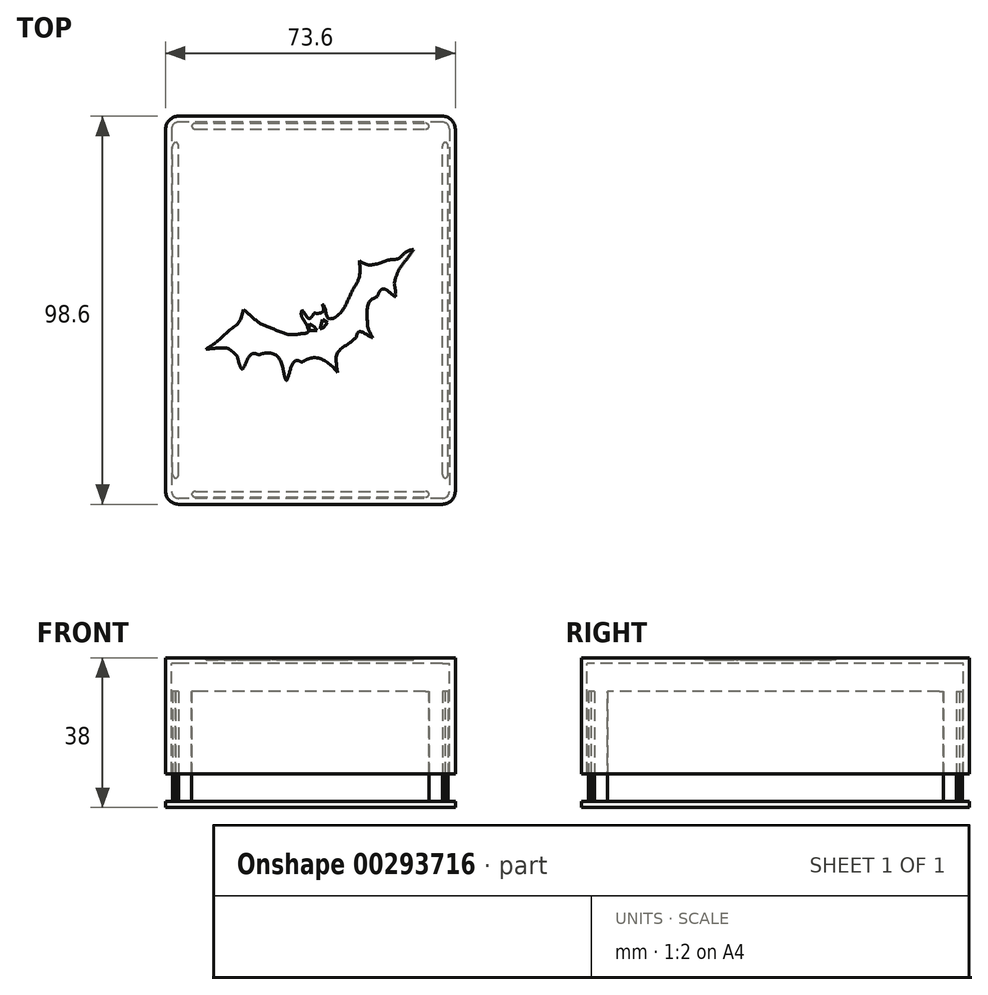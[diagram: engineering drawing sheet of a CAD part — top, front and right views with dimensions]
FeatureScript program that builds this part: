
annotation { "Feature Type Name" : "Feature", "Feature Type Description" : "" }
export const myFeature = defineFeature(function(context is Context, id is Id, definition is map)
    precondition{}
    {
        {
            assignVariable(context, id + "F0", {"name" : "DeckDepth", "anyValue" : 28});
        }
        {
            var Q0;
            Q0=qCreatedBy(makeId("Top.planeOp"),FACE);
            var sketch = newSketch(context, id + "F1", { "sketchPlane" : qUnion([Q0])});
            skLineSegment(sketch, "E0.bottom", {"start": v(33.5, 46) * mm, "end": v(-33.5, 46) * mm});
            skLineSegment(sketch, "E0.top", {"start": v(33.5, -46) * mm, "end": v(-33.5, -46) * mm});
            skLineSegment(sketch, "E0.left", {"start": v(33.5, 46) * mm, "end": v(33.5, -46) * mm});
            skLineSegment(sketch, "E0.right", {"start": v(-33.5, 46) * mm, "end": v(-33.5, -46) * mm});
            skPoint(sketch, "E0.middle", {"position": v(0, 0) * mm});
            skLineSegment(sketch, "E1.0", {"start": v(-35, 47.5) * mm, "end": v(-35, -47.5) * mm});
            skLineSegment(sketch, "E1.1", {"start": v(35, 47.5) * mm, "end": v(-35, 47.5) * mm});
            skLineSegment(sketch, "E1.2", {"start": v(35, 47.5) * mm, "end": v(35, -47.5) * mm});
            skLineSegment(sketch, "E1.3", {"start": v(35, -47.5) * mm, "end": v(-35, -47.5) * mm});
            skLineSegment(sketch, "E2.0", {"start": v(-36.8, 49.3) * mm, "end": v(-36.8, -49.3) * mm});
            skLineSegment(sketch, "E2.1", {"start": v(36.8, 49.3) * mm, "end": v(-36.8, 49.3) * mm});
            skLineSegment(sketch, "E2.2", {"start": v(36.8, 49.3) * mm, "end": v(36.8, -49.3) * mm});
            skLineSegment(sketch, "E2.3", {"start": v(36.8, -49.3) * mm, "end": v(-36.8, -49.3) * mm});
            skCircle(sketch, "E3", {"center": v(33.5, 46) * mm, "radius": 3.3 * mm});
            skCircle(sketch, "E4", {"center": v(33.5, 46) * mm, "radius": 1.5 * mm});
            skLineSegment(sketch, "E5", {"start": v(30.2, 46) * mm, "end": v(30.2, 47.5) * mm});
            skLineSegment(sketch, "E6", {"start": v(33.5, 42.7) * mm, "end": v(35, 42.7) * mm});
            skCircle(sketch, "E7", {"center": v(-33.5, 46) * mm, "radius": 3.3 * mm});
            skCircle(sketch, "E8", {"center": v(-33.5, 46) * mm, "radius": 1.5 * mm});
            skLineSegment(sketch, "E9", {"start": v(-30.2, 46) * mm, "end": v(-30.2, 47.5) * mm});
            skLineSegment(sketch, "E10", {"start": v(-33.5, 42.7) * mm, "end": v(-35, 42.7) * mm});
            skCircle(sketch, "E11", {"center": v(-33.5, -46) * mm, "radius": 3.3 * mm});
            skCircle(sketch, "E12", {"center": v(-33.5, -46) * mm, "radius": 1.5 * mm});
            skLineSegment(sketch, "E13", {"start": v(-33.5, -42.7) * mm, "end": v(-35, -42.7) * mm});
            skLineSegment(sketch, "E14", {"start": v(-30.2, -46) * mm, "end": v(-30.2, -47.5) * mm});
            skCircle(sketch, "E15", {"center": v(33.5, -46) * mm, "radius": 3.3 * mm});
            skCircle(sketch, "E16", {"center": v(33.5, -46) * mm, "radius": 1.5 * mm});
            skLineSegment(sketch, "E17", {"start": v(30.2, -46) * mm, "end": v(30.2, -47.5) * mm});
            skLineSegment(sketch, "E18", {"start": v(33.5, -42.7) * mm, "end": v(35, -42.7) * mm});
            skSolve(sketch);
        }
        {
            var Q0;
            {var subQ1=sQuery(id+"F1.wireOp",EDGE,"E1.0");var subQ5=sQuery(id+"F1.wireOp",EDGE,"E11");var subQ6=makeQuery(id+"F1.imprint","INTERSECT",VERTEX,{"derivedFrom":[subQ1,subQ5]});Q0=makeQuery(id+"F1.imprint","IMPRINT",FACE,{"disambiguationData":[TD([[makeQuery(id+"F1.imprint","IMPRINT",EDGE,{"disambiguationData":[TD([[subQ6,-1.0]])],"derivedFrom":subQ1}),-1.0]])]});}
            var Q1;
            {var subQ5=sQuery(id+"F1.wireOp",EDGE,"E3");var subQ13=sQuery(id+"F1.wireOp",EDGE,"E0.bottom");var subQ14=makeQuery(id+"F1.imprint","INTERSECT",VERTEX,{"derivedFrom":[subQ13,subQ5,sQuery(id+"F1.wireOp",EDGE,"E5")]});Q1=makeQuery(id+"F1.imprint","IMPRINT",FACE,{"disambiguationData":[TD([[makeQuery(id+"F1.imprint","IMPRINT",EDGE,{"disambiguationData":[TD([[subQ14,-1.0]])],"derivedFrom":subQ13}),1.0]])]});}
            var Q2;
            {var subQ0=sQuery(id+"F1.wireOp",EDGE,"E6");Q2=makeQuery(id+"F1.imprint","IMPRINT",FACE,{"disambiguationData":[TD([[makeQuery(id+"F1.imprint","IMPRINT",EDGE,{"derivedFrom":subQ0}),-1.0]])]});}
            var Q3;
            {var subQ0=sQuery(id+"F1.wireOp",EDGE,"E10");Q3=makeQuery(id+"F1.imprint","IMPRINT",FACE,{"disambiguationData":[TD([[makeQuery(id+"F1.imprint","IMPRINT",EDGE,{"derivedFrom":subQ0}),1.0]])]});}
            var Q4;
            {var subQ5=sQuery(id+"F1.wireOp",EDGE,"E1.2");var subQ8=makeQuery(id+"F1.imprint","INTERSECT",VERTEX,{"derivedFrom":[subQ5,sQuery(id+"F1.wireOp",EDGE,"E6")]});Q4=makeQuery(id+"F1.imprint","IMPRINT",FACE,{"disambiguationData":[TD([[makeQuery(id+"F1.imprint","IMPRINT",EDGE,{"disambiguationData":[TD([[subQ8,1.0]])],"derivedFrom":subQ5}),1.0]])]});}
            var Q5;
            {var subQ0=sQuery(id+"F1.wireOp",EDGE,"E1.3");var subQ8=makeQuery(id+"F1.imprint","INTERSECT",VERTEX,{"derivedFrom":[subQ0,sQuery(id+"F1.wireOp",EDGE,"E17")]});Q5=makeQuery(id+"F1.imprint","IMPRINT",FACE,{"disambiguationData":[TD([[makeQuery(id+"F1.imprint","IMPRINT",EDGE,{"disambiguationData":[TD([[subQ8,1.0]])],"derivedFrom":subQ0}),1.0]])]});}
            var Q6;
            {var subQ0=sQuery(id+"F1.wireOp",EDGE,"E5");Q6=makeQuery(id+"F1.imprint","IMPRINT",FACE,{"disambiguationData":[TD([[makeQuery(id+"F1.imprint","IMPRINT",EDGE,{"derivedFrom":subQ0}),1.0]])]});}
            var Q7;
            {var subQ1=sQuery(id+"F1.wireOp",EDGE,"E0.bottom");var subQ3=sQuery(id+"F1.wireOp",EDGE,"E4");var subQ4=makeQuery(id+"F1.imprint","INTERSECT",VERTEX,{"derivedFrom":[subQ1,subQ3]});Q7=makeQuery(id+"F1.imprint","IMPRINT",FACE,{"disambiguationData":[TD([[makeQuery(id+"F1.imprint","IMPRINT",EDGE,{"disambiguationData":[TD([[subQ4,-1.0]])],"derivedFrom":subQ3}),-1.0]])]});}
            var Q8;
            {var subQ1=sQuery(id+"F1.wireOp",EDGE,"E1.2");var subQ5=sQuery(id+"F1.wireOp",EDGE,"E1.1");var subQ6=makeQuery(id+"F1.imprint","INTERSECT",VERTEX,{"derivedFrom":[subQ5,subQ1]});Q8=makeQuery(id+"F1.imprint","IMPRINT",FACE,{"disambiguationData":[TD([[makeQuery(id+"F1.imprint","IMPRINT",EDGE,{"disambiguationData":[TD([[subQ6,-1.0]])],"derivedFrom":subQ5}),-1.0]])]});}
            var Q9;
            {var subQ0=sQuery(id+"F1.wireOp",EDGE,"E14");Q9=makeQuery(id+"F1.imprint","IMPRINT",FACE,{"disambiguationData":[TD([[makeQuery(id+"F1.imprint","IMPRINT",EDGE,{"derivedFrom":subQ0}),1.0]])]});}
            var Q10;
            {var subQ0=sQuery(id+"F1.wireOp",EDGE,"E1.1");var subQ1=sQuery(id+"F1.wireOp",EDGE,"E1.0");var subQ2=makeQuery(id+"F1.imprint","INTERSECT",VERTEX,{"derivedFrom":[subQ1,subQ0]});Q10=makeQuery(id+"F1.imprint","IMPRINT",FACE,{"disambiguationData":[TD([[makeQuery(id+"F1.imprint","IMPRINT",EDGE,{"disambiguationData":[TD([[subQ2,-1.0]])],"derivedFrom":subQ1}),-1.0]])]});}
            var Q11;
            {var subQ1=sQuery(id+"F1.wireOp",EDGE,"E0.top");var subQ3=sQuery(id+"F1.wireOp",EDGE,"E16");var subQ4=makeQuery(id+"F1.imprint","INTERSECT",VERTEX,{"derivedFrom":[subQ1,subQ3]});Q11=makeQuery(id+"F1.imprint","IMPRINT",FACE,{"disambiguationData":[TD([[makeQuery(id+"F1.imprint","IMPRINT",EDGE,{"disambiguationData":[TD([[subQ4,1.0]])],"derivedFrom":subQ3}),-1.0]])]});}
            var Q12;
            {var subQ5=sQuery(id+"F1.wireOp",EDGE,"E1.0");var subQ8=makeQuery(id+"F1.imprint","INTERSECT",VERTEX,{"derivedFrom":[subQ5,sQuery(id+"F1.wireOp",EDGE,"E10")]});Q12=makeQuery(id+"F1.imprint","IMPRINT",FACE,{"disambiguationData":[TD([[makeQuery(id+"F1.imprint","IMPRINT",EDGE,{"disambiguationData":[TD([[subQ8,1.0]])],"derivedFrom":subQ5}),-1.0]])]});}
            var Q13;
            {var subQ1=sQuery(id+"F1.wireOp",EDGE,"E0.bottom");var subQ3=sQuery(id+"F1.wireOp",EDGE,"E8");var subQ4=makeQuery(id+"F1.imprint","INTERSECT",VERTEX,{"derivedFrom":[subQ1,subQ3]});Q13=makeQuery(id+"F1.imprint","IMPRINT",FACE,{"disambiguationData":[TD([[makeQuery(id+"F1.imprint","IMPRINT",EDGE,{"disambiguationData":[TD([[subQ4,1.0]])],"derivedFrom":subQ3}),-1.0]])]});}
            var Q14;
            {var subQ1=sQuery(id+"F1.wireOp",EDGE,"E0.top");var subQ3=sQuery(id+"F1.wireOp",EDGE,"E12");var subQ4=makeQuery(id+"F1.imprint","INTERSECT",VERTEX,{"derivedFrom":[subQ1,subQ3]});Q14=makeQuery(id+"F1.imprint","IMPRINT",FACE,{"disambiguationData":[TD([[makeQuery(id+"F1.imprint","IMPRINT",EDGE,{"disambiguationData":[TD([[subQ4,-1.0]])],"derivedFrom":subQ3}),-1.0]])]});}
            var Q15;
            {var subQ5=sQuery(id+"F1.wireOp",EDGE,"E1.1");var subQ6=makeQuery(id+"F1.imprint","INTERSECT",VERTEX,{"derivedFrom":[subQ5,sQuery(id+"F1.wireOp",EDGE,"E5")]});Q15=makeQuery(id+"F1.imprint","IMPRINT",FACE,{"disambiguationData":[TD([[makeQuery(id+"F1.imprint","IMPRINT",EDGE,{"disambiguationData":[TD([[subQ6,1.0]])],"derivedFrom":subQ5}),-1.0]])]});}
            var Q16;
            {var subQ0=sQuery(id+"F1.wireOp",EDGE,"E7");var subQ5=sQuery(id+"F1.wireOp",EDGE,"E1.1");var subQ7=makeQuery(id+"F1.imprint","INTERSECT",VERTEX,{"derivedFrom":[subQ5,subQ0]});Q16=makeQuery(id+"F1.imprint","IMPRINT",FACE,{"disambiguationData":[TD([[makeQuery(id+"F1.imprint","IMPRINT",EDGE,{"disambiguationData":[TD([[subQ7,-1.0]])],"derivedFrom":subQ5}),1.0]])]});}
            var Q17;
            {var subQ3=sQuery(id+"F1.wireOp",EDGE,"E15");var subQ5=sQuery(id+"F1.wireOp",EDGE,"E1.2");var subQ8=makeQuery(id+"F1.imprint","INTERSECT",VERTEX,{"derivedFrom":[subQ5,subQ3]});Q17=makeQuery(id+"F1.imprint","IMPRINT",FACE,{"disambiguationData":[TD([[makeQuery(id+"F1.imprint","IMPRINT",EDGE,{"disambiguationData":[TD([[subQ8,-1.0]])],"derivedFrom":subQ5}),1.0]])]});}
            var Q18;
            {var subQ1=sQuery(id+"F1.wireOp",EDGE,"E0.bottom");var subQ5=sQuery(id+"F1.wireOp",EDGE,"E0.left");var subQ6=makeQuery(id+"F1.imprint","INTERSECT",VERTEX,{"derivedFrom":[subQ1,subQ5]});Q18=makeQuery(id+"F1.imprint","IMPRINT",FACE,{"disambiguationData":[TD([[makeQuery(id+"F1.imprint","IMPRINT",EDGE,{"disambiguationData":[TD([[subQ6,-1.0]])],"derivedFrom":subQ1}),-1.0]])]});}
            var Q19;
            {var subQ0=sQuery(id+"F1.wireOp",EDGE,"E11");var subQ5=sQuery(id+"F1.wireOp",EDGE,"E1.3");var subQ7=makeQuery(id+"F1.imprint","INTERSECT",VERTEX,{"derivedFrom":[subQ5,subQ0]});Q19=makeQuery(id+"F1.imprint","IMPRINT",FACE,{"disambiguationData":[TD([[makeQuery(id+"F1.imprint","IMPRINT",EDGE,{"disambiguationData":[TD([[subQ7,-1.0]])],"derivedFrom":subQ5}),-1.0]])]});}
            var Q20;
            {var subQ0=sQuery(id+"F1.wireOp",EDGE,"E15");var subQ5=sQuery(id+"F1.wireOp",EDGE,"E1.2");var subQ6=makeQuery(id+"F1.imprint","INTERSECT",VERTEX,{"derivedFrom":[subQ5,subQ0]});Q20=makeQuery(id+"F1.imprint","IMPRINT",FACE,{"disambiguationData":[TD([[makeQuery(id+"F1.imprint","IMPRINT",EDGE,{"disambiguationData":[TD([[subQ6,-1.0]])],"derivedFrom":subQ5}),-1.0]])]});}
            var Q21;
            {var subQ3=sQuery(id+"F1.wireOp",EDGE,"E4");var subQ5=sQuery(id+"F1.wireOp",EDGE,"E1.1");var subQ6=makeQuery(id+"F1.imprint","INTERSECT",VERTEX,{"derivedFrom":[subQ5,subQ3]});Q21=makeQuery(id+"F1.imprint","IMPRINT",FACE,{"disambiguationData":[TD([[makeQuery(id+"F1.imprint","IMPRINT",EDGE,{"disambiguationData":[TD([[subQ6,-1.0]])],"derivedFrom":subQ5}),1.0]])]});}
            var Q22;
            {var subQ1=sQuery(id+"F1.wireOp",EDGE,"E0.bottom");var subQ4=sQuery(id+"F1.wireOp",EDGE,"E0.right");var subQ5=makeQuery(id+"F1.imprint","INTERSECT",VERTEX,{"derivedFrom":[subQ1,subQ4]});Q22=makeQuery(id+"F1.imprint","IMPRINT",FACE,{"disambiguationData":[TD([[makeQuery(id+"F1.imprint","IMPRINT",EDGE,{"disambiguationData":[TD([[subQ5,1.0]])],"derivedFrom":subQ1}),-1.0]])]});}
            var Q23;
            {var subQ3=sQuery(id+"F1.wireOp",EDGE,"E16");var subQ5=sQuery(id+"F1.wireOp",EDGE,"E1.3");var subQ6=makeQuery(id+"F1.imprint","INTERSECT",VERTEX,{"derivedFrom":[subQ5,subQ3]});Q23=makeQuery(id+"F1.imprint","IMPRINT",FACE,{"disambiguationData":[TD([[makeQuery(id+"F1.imprint","IMPRINT",EDGE,{"disambiguationData":[TD([[subQ6,-1.0]])],"derivedFrom":subQ5}),-1.0]])]});}
            var Q24;
            {var subQ0=sQuery(id+"F1.wireOp",EDGE,"E6");Q24=makeQuery(id+"F1.imprint","IMPRINT",FACE,{"disambiguationData":[TD([[makeQuery(id+"F1.imprint","IMPRINT",EDGE,{"derivedFrom":subQ0}),1.0]])]});}
            var Q25;
            {var subQ0=sQuery(id+"F1.wireOp",EDGE,"E0.right");var subQ1=sQuery(id+"F1.wireOp",EDGE,"E0.top");var subQ2=makeQuery(id+"F1.imprint","INTERSECT",VERTEX,{"derivedFrom":[subQ1,subQ0]});Q25=makeQuery(id+"F1.imprint","IMPRINT",FACE,{"disambiguationData":[TD([[makeQuery(id+"F1.imprint","IMPRINT",EDGE,{"disambiguationData":[TD([[subQ2,1.0]])],"derivedFrom":subQ1}),-1.0]])]});}
            var Q26;
            {var subQ0=sQuery(id+"F1.wireOp",EDGE,"E0.left");var subQ1=sQuery(id+"F1.wireOp",EDGE,"E0.top");var subQ2=makeQuery(id+"F1.imprint","INTERSECT",VERTEX,{"derivedFrom":[subQ1,subQ0]});Q26=makeQuery(id+"F1.imprint","IMPRINT",FACE,{"disambiguationData":[TD([[makeQuery(id+"F1.imprint","IMPRINT",EDGE,{"disambiguationData":[TD([[subQ2,-1.0]])],"derivedFrom":subQ1}),-1.0]])]});}
            var Q27;
            {var subQ0=sQuery(id+"F1.wireOp",EDGE,"E11");var subQ5=sQuery(id+"F1.wireOp",EDGE,"E1.0");var subQ6=makeQuery(id+"F1.imprint","INTERSECT",VERTEX,{"derivedFrom":[subQ5,subQ0]});Q27=makeQuery(id+"F1.imprint","IMPRINT",FACE,{"disambiguationData":[TD([[makeQuery(id+"F1.imprint","IMPRINT",EDGE,{"disambiguationData":[TD([[subQ6,-1.0]])],"derivedFrom":subQ5}),1.0]])]});}
            var Q28;
            {var subQ3=sQuery(id+"F1.wireOp",EDGE,"E8");var subQ5=sQuery(id+"F1.wireOp",EDGE,"E1.0");var subQ6=makeQuery(id+"F1.imprint","INTERSECT",VERTEX,{"derivedFrom":[subQ5,subQ3]});Q28=makeQuery(id+"F1.imprint","IMPRINT",FACE,{"disambiguationData":[TD([[makeQuery(id+"F1.imprint","IMPRINT",EDGE,{"disambiguationData":[TD([[subQ6,-1.0]])],"derivedFrom":subQ5}),1.0]])]});}
            var Q29;
            {var subQ3=sQuery(id+"F1.wireOp",EDGE,"E0.right");var subQ5=sQuery(id+"F1.wireOp",EDGE,"E0.top");var subQ6=makeQuery(id+"F1.imprint","INTERSECT",VERTEX,{"derivedFrom":[subQ5,subQ3]});Q29=makeQuery(id+"F1.imprint","IMPRINT",FACE,{"disambiguationData":[TD([[makeQuery(id+"F1.imprint","IMPRINT",EDGE,{"disambiguationData":[TD([[subQ6,1.0]])],"derivedFrom":subQ5}),1.0]])]});}
            var Q30;
            {var subQ3=sQuery(id+"F1.wireOp",EDGE,"E4");var subQ5=sQuery(id+"F1.wireOp",EDGE,"E1.2");var subQ6=makeQuery(id+"F1.imprint","INTERSECT",VERTEX,{"derivedFrom":[subQ5,subQ3]});Q30=makeQuery(id+"F1.imprint","IMPRINT",FACE,{"disambiguationData":[TD([[makeQuery(id+"F1.imprint","IMPRINT",EDGE,{"disambiguationData":[TD([[subQ6,-1.0]])],"derivedFrom":subQ5}),-1.0]])]});}
            var Q31;
            {var subQ0=sQuery(id+"F1.wireOp",EDGE,"E14");Q31=makeQuery(id+"F1.imprint","IMPRINT",FACE,{"disambiguationData":[TD([[makeQuery(id+"F1.imprint","IMPRINT",EDGE,{"derivedFrom":subQ0}),-1.0]])]});}
            var Q32;
            {var subQ0=sQuery(id+"F1.wireOp",EDGE,"E9");Q32=makeQuery(id+"F1.imprint","IMPRINT",FACE,{"disambiguationData":[TD([[makeQuery(id+"F1.imprint","IMPRINT",EDGE,{"derivedFrom":subQ0}),1.0]])]});}
            var Q33;
            {var subQ0=sQuery(id+"F1.wireOp",EDGE,"E5");Q33=makeQuery(id+"F1.imprint","IMPRINT",FACE,{"disambiguationData":[TD([[makeQuery(id+"F1.imprint","IMPRINT",EDGE,{"derivedFrom":subQ0}),-1.0]])]});}
            var Q34;
            {var subQ0=sQuery(id+"F1.wireOp",EDGE,"E13");Q34=makeQuery(id+"F1.imprint","IMPRINT",FACE,{"disambiguationData":[TD([[makeQuery(id+"F1.imprint","IMPRINT",EDGE,{"derivedFrom":subQ0}),1.0]])]});}
            var Q35;
            {var subQ0=sQuery(id+"F1.wireOp",EDGE,"E0.left");var subQ1=sQuery(id+"F1.wireOp",EDGE,"E0.bottom");var subQ2=makeQuery(id+"F1.imprint","INTERSECT",VERTEX,{"derivedFrom":[subQ1,subQ0]});Q35=makeQuery(id+"F1.imprint","IMPRINT",FACE,{"disambiguationData":[TD([[makeQuery(id+"F1.imprint","IMPRINT",EDGE,{"disambiguationData":[TD([[subQ2,-1.0]])],"derivedFrom":subQ1}),1.0]])]});}
            var Q36;
            {var subQ0=sQuery(id+"F1.wireOp",EDGE,"E1.1");var subQ1=sQuery(id+"F1.wireOp",EDGE,"E1.0");var subQ2=makeQuery(id+"F1.imprint","INTERSECT",VERTEX,{"derivedFrom":[subQ1,subQ0]});Q36=makeQuery(id+"F1.imprint","IMPRINT",FACE,{"disambiguationData":[TD([[makeQuery(id+"F1.imprint","IMPRINT",EDGE,{"disambiguationData":[TD([[subQ2,-1.0]])],"derivedFrom":subQ1}),1.0]])]});}
            var Q37;
            {var subQ0=sQuery(id+"F1.wireOp",EDGE,"E1.3");var subQ1=sQuery(id+"F1.wireOp",EDGE,"E1.0");var subQ2=makeQuery(id+"F1.imprint","INTERSECT",VERTEX,{"derivedFrom":[subQ1,subQ0]});Q37=makeQuery(id+"F1.imprint","IMPRINT",FACE,{"disambiguationData":[TD([[makeQuery(id+"F1.imprint","IMPRINT",EDGE,{"disambiguationData":[TD([[subQ2,1.0]])],"derivedFrom":subQ1}),1.0]])]});}
            var Q38;
            {var subQ0=sQuery(id+"F1.wireOp",EDGE,"E1.2");var subQ1=sQuery(id+"F1.wireOp",EDGE,"E1.1");var subQ2=makeQuery(id+"F1.imprint","INTERSECT",VERTEX,{"derivedFrom":[subQ1,subQ0]});Q38=makeQuery(id+"F1.imprint","IMPRINT",FACE,{"disambiguationData":[TD([[makeQuery(id+"F1.imprint","IMPRINT",EDGE,{"disambiguationData":[TD([[subQ2,-1.0]])],"derivedFrom":subQ1}),1.0]])]});}
            var Q39;
            {var subQ0=sQuery(id+"F1.wireOp",EDGE,"E1.3");var subQ1=sQuery(id+"F1.wireOp",EDGE,"E1.2");var subQ2=makeQuery(id+"F1.imprint","INTERSECT",VERTEX,{"derivedFrom":[subQ1,subQ0]});Q39=makeQuery(id+"F1.imprint","IMPRINT",FACE,{"disambiguationData":[TD([[makeQuery(id+"F1.imprint","IMPRINT",EDGE,{"disambiguationData":[TD([[subQ2,1.0]])],"derivedFrom":subQ1}),-1.0]])]});}
            var Q40;
            {var subQ0=sQuery(id+"F1.wireOp",EDGE,"E10");Q40=makeQuery(id+"F1.imprint","IMPRINT",FACE,{"disambiguationData":[TD([[makeQuery(id+"F1.imprint","IMPRINT",EDGE,{"derivedFrom":subQ0}),-1.0]])]});}
            var Q41;
            {var subQ1=sQuery(id+"F1.wireOp",EDGE,"E0.left");var subQ4=sQuery(id+"F1.wireOp",EDGE,"E0.top");var subQ5=makeQuery(id+"F1.imprint","INTERSECT",VERTEX,{"derivedFrom":[subQ4,subQ1]});Q41=makeQuery(id+"F1.imprint","IMPRINT",FACE,{"disambiguationData":[TD([[makeQuery(id+"F1.imprint","IMPRINT",EDGE,{"disambiguationData":[TD([[subQ5,-1.0]])],"derivedFrom":subQ4}),1.0]])]});}
            var Q42;
            {var subQ0=sQuery(id+"F1.wireOp",EDGE,"E18");Q42=makeQuery(id+"F1.imprint","IMPRINT",FACE,{"disambiguationData":[TD([[makeQuery(id+"F1.imprint","IMPRINT",EDGE,{"derivedFrom":subQ0}),-1.0]])]});}
            var Q43;
            {var subQ0=sQuery(id+"F1.wireOp",EDGE,"E17");Q43=makeQuery(id+"F1.imprint","IMPRINT",FACE,{"disambiguationData":[TD([[makeQuery(id+"F1.imprint","IMPRINT",EDGE,{"derivedFrom":subQ0}),1.0]])]});}
            var Q44;
            {var subQ0=sQuery(id+"F1.wireOp",EDGE,"E0.right");var subQ1=sQuery(id+"F1.wireOp",EDGE,"E0.bottom");var subQ2=makeQuery(id+"F1.imprint","INTERSECT",VERTEX,{"derivedFrom":[subQ1,subQ0]});Q44=makeQuery(id+"F1.imprint","IMPRINT",FACE,{"disambiguationData":[TD([[makeQuery(id+"F1.imprint","IMPRINT",EDGE,{"disambiguationData":[TD([[subQ2,1.0]])],"derivedFrom":subQ1}),1.0]])]});}
            extrude(context, id + "F2", {"entities" : qUnion([Q0, Q1, Q2, Q3, Q4, Q5, Q6, Q7, Q8, Q9, Q10, Q11, Q12, Q13, Q14, Q15, Q16, Q17, Q18, Q19, Q20, Q21, Q22, Q23, Q24, Q25, Q26, Q27, Q28, Q29, Q30, Q31, Q32, Q33, Q34, Q35, Q36, Q37, Q38, Q39, Q40, Q41, Q42, Q43, Q44]), "depth" : 1.5 * mm});
        }
        {
            var Q0;
            {var subQ0=sQuery(id+"F1.wireOp",EDGE,"E10");Q0=makeQuery(id+"F1.imprint","IMPRINT",FACE,{"disambiguationData":[TD([[makeQuery(id+"F1.imprint","IMPRINT",EDGE,{"derivedFrom":subQ0}),1.0]])]});}
            var Q1;
            {var subQ0=sQuery(id+"F1.wireOp",EDGE,"E5");Q1=makeQuery(id+"F1.imprint","IMPRINT",FACE,{"disambiguationData":[TD([[makeQuery(id+"F1.imprint","IMPRINT",EDGE,{"derivedFrom":subQ0}),1.0]])]});}
            var Q2;
            {var subQ0=sQuery(id+"F1.wireOp",EDGE,"E6");Q2=makeQuery(id+"F1.imprint","IMPRINT",FACE,{"disambiguationData":[TD([[makeQuery(id+"F1.imprint","IMPRINT",EDGE,{"derivedFrom":subQ0}),-1.0]])]});}
            var Q3;
            {var subQ0=sQuery(id+"F1.wireOp",EDGE,"E14");Q3=makeQuery(id+"F1.imprint","IMPRINT",FACE,{"disambiguationData":[TD([[makeQuery(id+"F1.imprint","IMPRINT",EDGE,{"derivedFrom":subQ0}),1.0]])]});}
            extrude(context, id + "F3", {"entities" : qUnion([Q0, Q1, Q2, Q3]), "operationType" : NewBodyOperationType.ADD, "depth" : (1.5 + getVariable(context, 'DeckDepth')) * mm});
        }
        {
            var Q0;
            Q0=makeQuery(id+"F3.opExtrude","SWEPT_EDGE",EDGE,{"disambiguationData":[OSD([sQuery(id+"F1.wireOp",EDGE,"E0.left"),sQuery(id+"F1.wireOp",EDGE,"E15"),sQuery(id+"F1.wireOp",EDGE,"E18")])]});
            var Q1;
            Q1=makeQuery(id+"F3.opExtrude","SWEPT_EDGE",EDGE,{"disambiguationData":[OSD([sQuery(id+"F1.wireOp",EDGE,"E1.2"),sQuery(id+"F1.wireOp",EDGE,"E18")])]});
            var Q2;
            Q2=makeQuery(id+"F3.opExtrude","SWEPT_EDGE",EDGE,{"disambiguationData":[OSD([sQuery(id+"F1.wireOp",EDGE,"E0.top"),sQuery(id+"F1.wireOp",EDGE,"E15"),sQuery(id+"F1.wireOp",EDGE,"E17")])]});
            var Q3;
            Q3=makeQuery(id+"F3.opExtrude","SWEPT_EDGE",EDGE,{"disambiguationData":[OSD([sQuery(id+"F1.wireOp",EDGE,"E1.3"),sQuery(id+"F1.wireOp",EDGE,"E17")])]});
            var Q4;
            Q4=makeQuery(id+"F3.opExtrude","SWEPT_EDGE",EDGE,{"disambiguationData":[OSD([sQuery(id+"F1.wireOp",EDGE,"E1.3"),sQuery(id+"F1.wireOp",EDGE,"E14")])]});
            var Q5;
            Q5=makeQuery(id+"F3.opExtrude","SWEPT_EDGE",EDGE,{"disambiguationData":[OSD([sQuery(id+"F1.wireOp",EDGE,"E0.top"),sQuery(id+"F1.wireOp",EDGE,"E11"),sQuery(id+"F1.wireOp",EDGE,"E14")])]});
            var Q6;
            Q6=makeQuery(id+"F3.opExtrude","SWEPT_EDGE",EDGE,{"disambiguationData":[OSD([sQuery(id+"F1.wireOp",EDGE,"E1.0"),sQuery(id+"F1.wireOp",EDGE,"E13")])]});
            var Q7;
            Q7=makeQuery(id+"F3.opExtrude","SWEPT_EDGE",EDGE,{"disambiguationData":[OSD([sQuery(id+"F1.wireOp",EDGE,"E0.right"),sQuery(id+"F1.wireOp",EDGE,"E11"),sQuery(id+"F1.wireOp",EDGE,"E13")])]});
            var Q8;
            Q8=makeQuery(id+"F3.opExtrude","SWEPT_EDGE",EDGE,{"disambiguationData":[OSD([sQuery(id+"F1.wireOp",EDGE,"E1.0"),sQuery(id+"F1.wireOp",EDGE,"E10")])]});
            var Q9;
            Q9=makeQuery(id+"F3.opExtrude","SWEPT_EDGE",EDGE,{"disambiguationData":[OSD([sQuery(id+"F1.wireOp",EDGE,"E0.right"),sQuery(id+"F1.wireOp",EDGE,"E7"),sQuery(id+"F1.wireOp",EDGE,"E10")])]});
            var Q10;
            Q10=makeQuery(id+"F3.opExtrude","SWEPT_EDGE",EDGE,{"disambiguationData":[OSD([sQuery(id+"F1.wireOp",EDGE,"E0.bottom"),sQuery(id+"F1.wireOp",EDGE,"E7"),sQuery(id+"F1.wireOp",EDGE,"E9")])]});
            var Q11;
            Q11=makeQuery(id+"F3.opExtrude","SWEPT_EDGE",EDGE,{"disambiguationData":[OSD([sQuery(id+"F1.wireOp",EDGE,"E1.1"),sQuery(id+"F1.wireOp",EDGE,"E9")])]});
            var Q12;
            Q12=makeQuery(id+"F3.opExtrude","SWEPT_EDGE",EDGE,{"disambiguationData":[OSD([sQuery(id+"F1.wireOp",EDGE,"E1.1"),sQuery(id+"F1.wireOp",EDGE,"E5")])]});
            var Q13;
            Q13=makeQuery(id+"F3.opExtrude","SWEPT_EDGE",EDGE,{"disambiguationData":[OSD([sQuery(id+"F1.wireOp",EDGE,"E0.bottom"),sQuery(id+"F1.wireOp",EDGE,"E3"),sQuery(id+"F1.wireOp",EDGE,"E5")])]});
            var Q14;
            Q14=makeQuery(id+"F3.opExtrude","SWEPT_EDGE",EDGE,{"disambiguationData":[OSD([sQuery(id+"F1.wireOp",EDGE,"E0.left"),sQuery(id+"F1.wireOp",EDGE,"E3"),sQuery(id+"F1.wireOp",EDGE,"E6")])]});
            var Q15;
            Q15=makeQuery(id+"F3.opExtrude","SWEPT_EDGE",EDGE,{"disambiguationData":[OSD([sQuery(id+"F1.wireOp",EDGE,"E1.2"),sQuery(id+"F1.wireOp",EDGE,"E6")])]});
            fillet(context, id + "F4", {"entities" : qUnion([Q0, Q1, Q2, Q3, Q4, Q5, Q6, Q7, Q8, Q9, Q10, Q11, Q12, Q13, Q14, Q15]), "radius" : 1 * mm, "tangentPropagation" : true, "allowEdgeOverflow" : false});
        }
        {
            var Q0;
            {var subQ5=sQuery(id+"F1.wireOp",EDGE,"E3");var subQ13=sQuery(id+"F1.wireOp",EDGE,"E0.bottom");var subQ14=makeQuery(id+"F1.imprint","INTERSECT",VERTEX,{"derivedFrom":[subQ13,subQ5,sQuery(id+"F1.wireOp",EDGE,"E5")]});Q0=makeQuery(id+"F1.imprint","IMPRINT",FACE,{"disambiguationData":[TD([[makeQuery(id+"F1.imprint","IMPRINT",EDGE,{"disambiguationData":[TD([[subQ14,-1.0]])],"derivedFrom":subQ13}),1.0]])]});}
            var Q1;
            {var subQ0=sQuery(id+"F1.wireOp",EDGE,"E1.1");var subQ1=sQuery(id+"F1.wireOp",EDGE,"E1.0");var subQ2=makeQuery(id+"F1.imprint","INTERSECT",VERTEX,{"derivedFrom":[subQ1,subQ0]});Q1=makeQuery(id+"F1.imprint","IMPRINT",FACE,{"disambiguationData":[TD([[makeQuery(id+"F1.imprint","IMPRINT",EDGE,{"disambiguationData":[TD([[subQ2,-1.0]])],"derivedFrom":subQ1}),-1.0]])]});}
            var Q2;
            {var subQ0=sQuery(id+"F1.wireOp",EDGE,"E1.3");var subQ8=makeQuery(id+"F1.imprint","INTERSECT",VERTEX,{"derivedFrom":[subQ0,sQuery(id+"F1.wireOp",EDGE,"E17")]});Q2=makeQuery(id+"F1.imprint","IMPRINT",FACE,{"disambiguationData":[TD([[makeQuery(id+"F1.imprint","IMPRINT",EDGE,{"disambiguationData":[TD([[subQ8,1.0]])],"derivedFrom":subQ0}),1.0]])]});}
            var Q3;
            {var subQ1=sQuery(id+"F1.wireOp",EDGE,"E0.bottom");var subQ3=sQuery(id+"F1.wireOp",EDGE,"E4");var subQ4=makeQuery(id+"F1.imprint","INTERSECT",VERTEX,{"derivedFrom":[subQ1,subQ3]});Q3=makeQuery(id+"F1.imprint","IMPRINT",FACE,{"disambiguationData":[TD([[makeQuery(id+"F1.imprint","IMPRINT",EDGE,{"disambiguationData":[TD([[subQ4,-1.0]])],"derivedFrom":subQ3}),-1.0]])]});}
            var Q4;
            {var subQ0=sQuery(id+"F1.wireOp",EDGE,"E5");Q4=makeQuery(id+"F1.imprint","IMPRINT",FACE,{"disambiguationData":[TD([[makeQuery(id+"F1.imprint","IMPRINT",EDGE,{"derivedFrom":subQ0}),1.0]])]});}
            var Q5;
            {var subQ1=sQuery(id+"F1.wireOp",EDGE,"E1.0");var subQ5=sQuery(id+"F1.wireOp",EDGE,"E11");var subQ6=makeQuery(id+"F1.imprint","INTERSECT",VERTEX,{"derivedFrom":[subQ1,subQ5]});Q5=makeQuery(id+"F1.imprint","IMPRINT",FACE,{"disambiguationData":[TD([[makeQuery(id+"F1.imprint","IMPRINT",EDGE,{"disambiguationData":[TD([[subQ6,-1.0]])],"derivedFrom":subQ1}),-1.0]])]});}
            var Q6;
            {var subQ0=sQuery(id+"F1.wireOp",EDGE,"E14");Q6=makeQuery(id+"F1.imprint","IMPRINT",FACE,{"disambiguationData":[TD([[makeQuery(id+"F1.imprint","IMPRINT",EDGE,{"derivedFrom":subQ0}),1.0]])]});}
            var Q7;
            {var subQ1=sQuery(id+"F1.wireOp",EDGE,"E1.2");var subQ5=sQuery(id+"F1.wireOp",EDGE,"E1.1");var subQ6=makeQuery(id+"F1.imprint","INTERSECT",VERTEX,{"derivedFrom":[subQ5,subQ1]});Q7=makeQuery(id+"F1.imprint","IMPRINT",FACE,{"disambiguationData":[TD([[makeQuery(id+"F1.imprint","IMPRINT",EDGE,{"disambiguationData":[TD([[subQ6,-1.0]])],"derivedFrom":subQ5}),-1.0]])]});}
            var Q8;
            {var subQ1=sQuery(id+"F1.wireOp",EDGE,"E0.top");var subQ3=sQuery(id+"F1.wireOp",EDGE,"E16");var subQ4=makeQuery(id+"F1.imprint","INTERSECT",VERTEX,{"derivedFrom":[subQ1,subQ3]});Q8=makeQuery(id+"F1.imprint","IMPRINT",FACE,{"disambiguationData":[TD([[makeQuery(id+"F1.imprint","IMPRINT",EDGE,{"disambiguationData":[TD([[subQ4,1.0]])],"derivedFrom":subQ3}),-1.0]])]});}
            var Q9;
            {var subQ5=sQuery(id+"F1.wireOp",EDGE,"E1.0");var subQ8=makeQuery(id+"F1.imprint","INTERSECT",VERTEX,{"derivedFrom":[subQ5,sQuery(id+"F1.wireOp",EDGE,"E10")]});Q9=makeQuery(id+"F1.imprint","IMPRINT",FACE,{"disambiguationData":[TD([[makeQuery(id+"F1.imprint","IMPRINT",EDGE,{"disambiguationData":[TD([[subQ8,1.0]])],"derivedFrom":subQ5}),-1.0]])]});}
            var Q10;
            {var subQ0=sQuery(id+"F1.wireOp",EDGE,"E10");Q10=makeQuery(id+"F1.imprint","IMPRINT",FACE,{"disambiguationData":[TD([[makeQuery(id+"F1.imprint","IMPRINT",EDGE,{"derivedFrom":subQ0}),1.0]])]});}
            var Q11;
            {var subQ1=sQuery(id+"F1.wireOp",EDGE,"E0.bottom");var subQ3=sQuery(id+"F1.wireOp",EDGE,"E8");var subQ4=makeQuery(id+"F1.imprint","INTERSECT",VERTEX,{"derivedFrom":[subQ1,subQ3]});Q11=makeQuery(id+"F1.imprint","IMPRINT",FACE,{"disambiguationData":[TD([[makeQuery(id+"F1.imprint","IMPRINT",EDGE,{"disambiguationData":[TD([[subQ4,1.0]])],"derivedFrom":subQ3}),-1.0]])]});}
            var Q12;
            {var subQ5=sQuery(id+"F1.wireOp",EDGE,"E1.2");var subQ8=makeQuery(id+"F1.imprint","INTERSECT",VERTEX,{"derivedFrom":[subQ5,sQuery(id+"F1.wireOp",EDGE,"E6")]});Q12=makeQuery(id+"F1.imprint","IMPRINT",FACE,{"disambiguationData":[TD([[makeQuery(id+"F1.imprint","IMPRINT",EDGE,{"disambiguationData":[TD([[subQ8,1.0]])],"derivedFrom":subQ5}),1.0]])]});}
            var Q13;
            {var subQ1=sQuery(id+"F1.wireOp",EDGE,"E0.top");var subQ3=sQuery(id+"F1.wireOp",EDGE,"E12");var subQ4=makeQuery(id+"F1.imprint","INTERSECT",VERTEX,{"derivedFrom":[subQ1,subQ3]});Q13=makeQuery(id+"F1.imprint","IMPRINT",FACE,{"disambiguationData":[TD([[makeQuery(id+"F1.imprint","IMPRINT",EDGE,{"disambiguationData":[TD([[subQ4,-1.0]])],"derivedFrom":subQ3}),-1.0]])]});}
            var Q14;
            {var subQ0=sQuery(id+"F1.wireOp",EDGE,"E6");Q14=makeQuery(id+"F1.imprint","IMPRINT",FACE,{"disambiguationData":[TD([[makeQuery(id+"F1.imprint","IMPRINT",EDGE,{"derivedFrom":subQ0}),-1.0]])]});}
            var Q15;
            {var subQ5=sQuery(id+"F1.wireOp",EDGE,"E1.1");var subQ6=makeQuery(id+"F1.imprint","INTERSECT",VERTEX,{"derivedFrom":[subQ5,sQuery(id+"F1.wireOp",EDGE,"E5")]});Q15=makeQuery(id+"F1.imprint","IMPRINT",FACE,{"disambiguationData":[TD([[makeQuery(id+"F1.imprint","IMPRINT",EDGE,{"disambiguationData":[TD([[subQ6,1.0]])],"derivedFrom":subQ5}),-1.0]])]});}
            var Q16;
            {var subQ3=sQuery(id+"F1.wireOp",EDGE,"E15");var subQ5=sQuery(id+"F1.wireOp",EDGE,"E1.2");var subQ8=makeQuery(id+"F1.imprint","INTERSECT",VERTEX,{"derivedFrom":[subQ5,subQ3]});Q16=makeQuery(id+"F1.imprint","IMPRINT",FACE,{"disambiguationData":[TD([[makeQuery(id+"F1.imprint","IMPRINT",EDGE,{"disambiguationData":[TD([[subQ8,-1.0]])],"derivedFrom":subQ5}),1.0]])]});}
            var Q17;
            {var subQ0=sQuery(id+"F1.wireOp",EDGE,"E11");var subQ5=sQuery(id+"F1.wireOp",EDGE,"E1.0");var subQ6=makeQuery(id+"F1.imprint","INTERSECT",VERTEX,{"derivedFrom":[subQ5,subQ0]});Q17=makeQuery(id+"F1.imprint","IMPRINT",FACE,{"disambiguationData":[TD([[makeQuery(id+"F1.imprint","IMPRINT",EDGE,{"disambiguationData":[TD([[subQ6,-1.0]])],"derivedFrom":subQ5}),1.0]])]});}
            var Q18;
            {var subQ0=sQuery(id+"F1.wireOp",EDGE,"E15");var subQ5=sQuery(id+"F1.wireOp",EDGE,"E1.2");var subQ6=makeQuery(id+"F1.imprint","INTERSECT",VERTEX,{"derivedFrom":[subQ5,subQ0]});Q18=makeQuery(id+"F1.imprint","IMPRINT",FACE,{"disambiguationData":[TD([[makeQuery(id+"F1.imprint","IMPRINT",EDGE,{"disambiguationData":[TD([[subQ6,-1.0]])],"derivedFrom":subQ5}),-1.0]])]});}
            var Q19;
            {var subQ0=sQuery(id+"F1.wireOp",EDGE,"E11");var subQ5=sQuery(id+"F1.wireOp",EDGE,"E1.3");var subQ7=makeQuery(id+"F1.imprint","INTERSECT",VERTEX,{"derivedFrom":[subQ5,subQ0]});Q19=makeQuery(id+"F1.imprint","IMPRINT",FACE,{"disambiguationData":[TD([[makeQuery(id+"F1.imprint","IMPRINT",EDGE,{"disambiguationData":[TD([[subQ7,-1.0]])],"derivedFrom":subQ5}),-1.0]])]});}
            var Q20;
            {var subQ3=sQuery(id+"F1.wireOp",EDGE,"E8");var subQ5=sQuery(id+"F1.wireOp",EDGE,"E1.0");var subQ6=makeQuery(id+"F1.imprint","INTERSECT",VERTEX,{"derivedFrom":[subQ5,subQ3]});Q20=makeQuery(id+"F1.imprint","IMPRINT",FACE,{"disambiguationData":[TD([[makeQuery(id+"F1.imprint","IMPRINT",EDGE,{"disambiguationData":[TD([[subQ6,-1.0]])],"derivedFrom":subQ5}),1.0]])]});}
            var Q21;
            {var subQ0=sQuery(id+"F1.wireOp",EDGE,"E0.left");var subQ1=sQuery(id+"F1.wireOp",EDGE,"E0.bottom");var subQ2=makeQuery(id+"F1.imprint","INTERSECT",VERTEX,{"derivedFrom":[subQ1,subQ0]});Q21=makeQuery(id+"F1.imprint","IMPRINT",FACE,{"disambiguationData":[TD([[makeQuery(id+"F1.imprint","IMPRINT",EDGE,{"disambiguationData":[TD([[subQ2,-1.0]])],"derivedFrom":subQ1}),1.0]])]});}
            var Q22;
            {var subQ3=sQuery(id+"F1.wireOp",EDGE,"E16");var subQ5=sQuery(id+"F1.wireOp",EDGE,"E1.3");var subQ6=makeQuery(id+"F1.imprint","INTERSECT",VERTEX,{"derivedFrom":[subQ5,subQ3]});Q22=makeQuery(id+"F1.imprint","IMPRINT",FACE,{"disambiguationData":[TD([[makeQuery(id+"F1.imprint","IMPRINT",EDGE,{"disambiguationData":[TD([[subQ6,-1.0]])],"derivedFrom":subQ5}),-1.0]])]});}
            var Q23;
            {var subQ0=sQuery(id+"F1.wireOp",EDGE,"E0.right");var subQ1=sQuery(id+"F1.wireOp",EDGE,"E0.bottom");var subQ2=makeQuery(id+"F1.imprint","INTERSECT",VERTEX,{"derivedFrom":[subQ1,subQ0]});Q23=makeQuery(id+"F1.imprint","IMPRINT",FACE,{"disambiguationData":[TD([[makeQuery(id+"F1.imprint","IMPRINT",EDGE,{"disambiguationData":[TD([[subQ2,1.0]])],"derivedFrom":subQ1}),1.0]])]});}
            var Q24;
            {var subQ0=sQuery(id+"F1.wireOp",EDGE,"E0.right");var subQ1=sQuery(id+"F1.wireOp",EDGE,"E0.top");var subQ2=makeQuery(id+"F1.imprint","INTERSECT",VERTEX,{"derivedFrom":[subQ1,subQ0]});Q24=makeQuery(id+"F1.imprint","IMPRINT",FACE,{"disambiguationData":[TD([[makeQuery(id+"F1.imprint","IMPRINT",EDGE,{"disambiguationData":[TD([[subQ2,1.0]])],"derivedFrom":subQ1}),-1.0]])]});}
            var Q25;
            {var subQ0=sQuery(id+"F1.wireOp",EDGE,"E9");Q25=makeQuery(id+"F1.imprint","IMPRINT",FACE,{"disambiguationData":[TD([[makeQuery(id+"F1.imprint","IMPRINT",EDGE,{"derivedFrom":subQ0}),1.0]])]});}
            var Q26;
            {var subQ1=sQuery(id+"F1.wireOp",EDGE,"E0.bottom");var subQ5=sQuery(id+"F1.wireOp",EDGE,"E0.left");var subQ6=makeQuery(id+"F1.imprint","INTERSECT",VERTEX,{"derivedFrom":[subQ1,subQ5]});Q26=makeQuery(id+"F1.imprint","IMPRINT",FACE,{"disambiguationData":[TD([[makeQuery(id+"F1.imprint","IMPRINT",EDGE,{"disambiguationData":[TD([[subQ6,-1.0]])],"derivedFrom":subQ1}),-1.0]])]});}
            var Q27;
            {var subQ3=sQuery(id+"F1.wireOp",EDGE,"E4");var subQ5=sQuery(id+"F1.wireOp",EDGE,"E1.1");var subQ6=makeQuery(id+"F1.imprint","INTERSECT",VERTEX,{"derivedFrom":[subQ5,subQ3]});Q27=makeQuery(id+"F1.imprint","IMPRINT",FACE,{"disambiguationData":[TD([[makeQuery(id+"F1.imprint","IMPRINT",EDGE,{"disambiguationData":[TD([[subQ6,-1.0]])],"derivedFrom":subQ5}),1.0]])]});}
            var Q28;
            {var subQ1=sQuery(id+"F1.wireOp",EDGE,"E0.bottom");var subQ4=sQuery(id+"F1.wireOp",EDGE,"E0.right");var subQ5=makeQuery(id+"F1.imprint","INTERSECT",VERTEX,{"derivedFrom":[subQ1,subQ4]});Q28=makeQuery(id+"F1.imprint","IMPRINT",FACE,{"disambiguationData":[TD([[makeQuery(id+"F1.imprint","IMPRINT",EDGE,{"disambiguationData":[TD([[subQ5,1.0]])],"derivedFrom":subQ1}),-1.0]])]});}
            var Q29;
            {var subQ3=sQuery(id+"F1.wireOp",EDGE,"E4");var subQ5=sQuery(id+"F1.wireOp",EDGE,"E1.2");var subQ6=makeQuery(id+"F1.imprint","INTERSECT",VERTEX,{"derivedFrom":[subQ5,subQ3]});Q29=makeQuery(id+"F1.imprint","IMPRINT",FACE,{"disambiguationData":[TD([[makeQuery(id+"F1.imprint","IMPRINT",EDGE,{"disambiguationData":[TD([[subQ6,-1.0]])],"derivedFrom":subQ5}),-1.0]])]});}
            var Q30;
            {var subQ0=sQuery(id+"F1.wireOp",EDGE,"E14");Q30=makeQuery(id+"F1.imprint","IMPRINT",FACE,{"disambiguationData":[TD([[makeQuery(id+"F1.imprint","IMPRINT",EDGE,{"derivedFrom":subQ0}),-1.0]])]});}
            var Q31;
            {var subQ0=sQuery(id+"F1.wireOp",EDGE,"E7");var subQ5=sQuery(id+"F1.wireOp",EDGE,"E1.1");var subQ7=makeQuery(id+"F1.imprint","INTERSECT",VERTEX,{"derivedFrom":[subQ5,subQ0]});Q31=makeQuery(id+"F1.imprint","IMPRINT",FACE,{"disambiguationData":[TD([[makeQuery(id+"F1.imprint","IMPRINT",EDGE,{"disambiguationData":[TD([[subQ7,-1.0]])],"derivedFrom":subQ5}),1.0]])]});}
            var Q32;
            {var subQ0=sQuery(id+"F1.wireOp",EDGE,"E10");Q32=makeQuery(id+"F1.imprint","IMPRINT",FACE,{"disambiguationData":[TD([[makeQuery(id+"F1.imprint","IMPRINT",EDGE,{"derivedFrom":subQ0}),-1.0]])]});}
            var Q33;
            {var subQ1=sQuery(id+"F1.wireOp",EDGE,"E0.left");var subQ4=sQuery(id+"F1.wireOp",EDGE,"E0.top");var subQ5=makeQuery(id+"F1.imprint","INTERSECT",VERTEX,{"derivedFrom":[subQ4,subQ1]});Q33=makeQuery(id+"F1.imprint","IMPRINT",FACE,{"disambiguationData":[TD([[makeQuery(id+"F1.imprint","IMPRINT",EDGE,{"disambiguationData":[TD([[subQ5,-1.0]])],"derivedFrom":subQ4}),1.0]])]});}
            var Q34;
            {var subQ0=sQuery(id+"F1.wireOp",EDGE,"E0.left");var subQ1=sQuery(id+"F1.wireOp",EDGE,"E0.top");var subQ2=makeQuery(id+"F1.imprint","INTERSECT",VERTEX,{"derivedFrom":[subQ1,subQ0]});Q34=makeQuery(id+"F1.imprint","IMPRINT",FACE,{"disambiguationData":[TD([[makeQuery(id+"F1.imprint","IMPRINT",EDGE,{"disambiguationData":[TD([[subQ2,-1.0]])],"derivedFrom":subQ1}),-1.0]])]});}
            var Q35;
            {var subQ0=sQuery(id+"F1.wireOp",EDGE,"E1.1");var subQ1=sQuery(id+"F1.wireOp",EDGE,"E1.0");var subQ2=makeQuery(id+"F1.imprint","INTERSECT",VERTEX,{"derivedFrom":[subQ1,subQ0]});Q35=makeQuery(id+"F1.imprint","IMPRINT",FACE,{"disambiguationData":[TD([[makeQuery(id+"F1.imprint","IMPRINT",EDGE,{"disambiguationData":[TD([[subQ2,-1.0]])],"derivedFrom":subQ1}),1.0]])]});}
            var Q36;
            {var subQ0=sQuery(id+"F1.wireOp",EDGE,"E1.3");var subQ1=sQuery(id+"F1.wireOp",EDGE,"E1.0");var subQ2=makeQuery(id+"F1.imprint","INTERSECT",VERTEX,{"derivedFrom":[subQ1,subQ0]});Q36=makeQuery(id+"F1.imprint","IMPRINT",FACE,{"disambiguationData":[TD([[makeQuery(id+"F1.imprint","IMPRINT",EDGE,{"disambiguationData":[TD([[subQ2,1.0]])],"derivedFrom":subQ1}),1.0]])]});}
            var Q37;
            {var subQ0=sQuery(id+"F1.wireOp",EDGE,"E13");Q37=makeQuery(id+"F1.imprint","IMPRINT",FACE,{"disambiguationData":[TD([[makeQuery(id+"F1.imprint","IMPRINT",EDGE,{"derivedFrom":subQ0}),1.0]])]});}
            var Q38;
            {var subQ0=sQuery(id+"F1.wireOp",EDGE,"E5");Q38=makeQuery(id+"F1.imprint","IMPRINT",FACE,{"disambiguationData":[TD([[makeQuery(id+"F1.imprint","IMPRINT",EDGE,{"derivedFrom":subQ0}),-1.0]])]});}
            var Q39;
            {var subQ0=sQuery(id+"F1.wireOp",EDGE,"E6");Q39=makeQuery(id+"F1.imprint","IMPRINT",FACE,{"disambiguationData":[TD([[makeQuery(id+"F1.imprint","IMPRINT",EDGE,{"derivedFrom":subQ0}),1.0]])]});}
            var Q40;
            {var subQ3=sQuery(id+"F1.wireOp",EDGE,"E0.right");var subQ5=sQuery(id+"F1.wireOp",EDGE,"E0.top");var subQ6=makeQuery(id+"F1.imprint","INTERSECT",VERTEX,{"derivedFrom":[subQ5,subQ3]});Q40=makeQuery(id+"F1.imprint","IMPRINT",FACE,{"disambiguationData":[TD([[makeQuery(id+"F1.imprint","IMPRINT",EDGE,{"disambiguationData":[TD([[subQ6,1.0]])],"derivedFrom":subQ5}),1.0]])]});}
            var Q41;
            {var subQ0=sQuery(id+"F1.wireOp",EDGE,"E18");Q41=makeQuery(id+"F1.imprint","IMPRINT",FACE,{"disambiguationData":[TD([[makeQuery(id+"F1.imprint","IMPRINT",EDGE,{"derivedFrom":subQ0}),-1.0]])]});}
            var Q42;
            {var subQ0=sQuery(id+"F1.wireOp",EDGE,"E17");Q42=makeQuery(id+"F1.imprint","IMPRINT",FACE,{"disambiguationData":[TD([[makeQuery(id+"F1.imprint","IMPRINT",EDGE,{"derivedFrom":subQ0}),1.0]])]});}
            var Q43;
            {var subQ0=sQuery(id+"F1.wireOp",EDGE,"E1.2");var subQ1=sQuery(id+"F1.wireOp",EDGE,"E1.1");var subQ2=makeQuery(id+"F1.imprint","INTERSECT",VERTEX,{"derivedFrom":[subQ1,subQ0]});Q43=makeQuery(id+"F1.imprint","IMPRINT",FACE,{"disambiguationData":[TD([[makeQuery(id+"F1.imprint","IMPRINT",EDGE,{"disambiguationData":[TD([[subQ2,-1.0]])],"derivedFrom":subQ1}),1.0]])]});}
            var Q44;
            {var subQ0=sQuery(id+"F1.wireOp",EDGE,"E1.3");var subQ1=sQuery(id+"F1.wireOp",EDGE,"E1.2");var subQ2=makeQuery(id+"F1.imprint","INTERSECT",VERTEX,{"derivedFrom":[subQ1,subQ0]});Q44=makeQuery(id+"F1.imprint","IMPRINT",FACE,{"disambiguationData":[TD([[makeQuery(id+"F1.imprint","IMPRINT",EDGE,{"disambiguationData":[TD([[subQ2,1.0]])],"derivedFrom":subQ1}),-1.0]])]});}
            extrude(context, id + "F5", {"entities" : qUnion([Q0, Q1, Q2, Q3, Q4, Q5, Q6, Q7, Q8, Q9, Q10, Q11, Q12, Q13, Q14, Q15, Q16, Q17, Q18, Q19, Q20, Q21, Q22, Q23, Q24, Q25, Q26, Q27, Q28, Q29, Q30, Q31, Q32, Q33, Q34, Q35, Q36, Q37, Q38, Q39, Q40, Q41, Q42, Q43, Q44]), "oppositeDirection" : true, "depth" : (1.5 + getVariable(context, 'DeckDepth')) * mm});
        }
        {
            var Q0;
            Q0=makeQuery(id+"F5.opExtrude","SWEPT_BODY",BODY,{"disambiguationData":[OSD([sQuery(id+"F1.wireOp",EDGE,"E2.0"),sQuery(id+"F1.wireOp",EDGE,"E2.1"),sQuery(id+"F1.wireOp",EDGE,"E2.2"),sQuery(id+"F1.wireOp",EDGE,"E2.3"),sQuery(id+"F1.wireOp",EDGE,"E3"),sQuery(id+"F1.wireOp",EDGE,"E7"),sQuery(id+"F1.wireOp",EDGE,"E11"),sQuery(id+"F1.wireOp",EDGE,"E15")])]});
            transform(context, id + "F6", {"entities" : qUnion([Q0]), "transformType" : TransformType.TRANSLATION_3D, "dx" : 0 * mm, "dy" : 0 * mm, "dz" : (getVariable(context, 'DeckDepth') + 10) * mm, "makeCopy" : false});
        }
        {
            var Q0;
            Q0=makeQuery(id+"F5.opExtrude","CAP_FACE",FACE,{"disambiguationData":[OSD([sQuery(id+"F1.wireOp",EDGE,"E2.0"),sQuery(id+"F1.wireOp",EDGE,"E2.1"),sQuery(id+"F1.wireOp",EDGE,"E2.2"),sQuery(id+"F1.wireOp",EDGE,"E2.3"),sQuery(id+"F1.wireOp",EDGE,"E3"),sQuery(id+"F1.wireOp",EDGE,"E7"),sQuery(id+"F1.wireOp",EDGE,"E11"),sQuery(id+"F1.wireOp",EDGE,"E15")])],"isStart":false});
            shell(context, id + "F7", {"entities" : qUnion([Q0]), "thickness" : 1.5 * mm});
        }
        {
            var Q0;
            Q0=makeQuery(id+"F5.opExtrude","CAP_FACE",FACE,{"disambiguationData":[OSD([sQuery(id+"F1.wireOp",EDGE,"E2.0"),sQuery(id+"F1.wireOp",EDGE,"E2.1"),sQuery(id+"F1.wireOp",EDGE,"E2.2"),sQuery(id+"F1.wireOp",EDGE,"E2.3"),sQuery(id+"F1.wireOp",EDGE,"E3"),sQuery(id+"F1.wireOp",EDGE,"E7"),sQuery(id+"F1.wireOp",EDGE,"E11"),sQuery(id+"F1.wireOp",EDGE,"E15")])],"isStart":true});
            var sketch = newSketch(context, id + "F8", { "sketchPlane" : qUnion([Q0])});
            skFitSpline(sketch, "E19", {"points": [v(-26.63, -9.85) * mm, v(-23.9, -9.65) * mm, v(-20.97, -9.77) * mm, v(-18.57, -11.75) * mm]});
            skFitSpline(sketch, "E20", {"points": [v(-18.57, -11.75) * mm, v(-17.22, -14.97) * mm, v(-15.1, -11.3) * mm, v(-13.18, -11.32) * mm]});
            skFitSpline(sketch, "E21", {"points": [v(-13.18, -11.32) * mm, v(-10.8, -10.87) * mm, v(-8.3, -11.83) * mm, v(-7, -14.76) * mm]});
            skFitSpline(sketch, "E22", {"points": [v(-7, -14.76) * mm, v(-5.95, -17.84) * mm, v(-4.01, -12.99) * mm, v(-2.26, -13.23) * mm]});
            skFitSpline(sketch, "E23", {"points": [v(-2.26, -13.23) * mm, v(0.98, -12.06) * mm, v(4.54, -13.43) * mm, v(7.14, -16.12) * mm]});
            skFitSpline(sketch, "E24", {"points": [v(7.14, -16.12) * mm, v(7.05, -12.21) * mm, v(9.74, -9.68) * mm, v(11.94, -7.8) * mm]});
            skFitSpline(sketch, "E25", {"points": [v(11.94, -7.8) * mm, v(12.94, -6.2) * mm, v(16.08, -7.82) * mm, v(14.89, -4.83) * mm]});
            skFitSpline(sketch, "E26", {"points": [v(14.89, -4.83) * mm, v(14.75, -1.82) * mm, v(15.22, 1.75) * mm, v(17.37, 3.34) * mm]});
            skFitSpline(sketch, "E27", {"points": [v(17.37, 3.34) * mm, v(18.82, 5.35) * mm, v(21.8, 3.33) * mm, v(21.68, 6.93) * mm]});
            skFitSpline(sketch, "E28", {"points": [v(21.68, 6.93) * mm, v(22.83, 10.5) * mm, v(24.84, 13.39) * mm, v(26.8, 16.2) * mm]});
            skFitSpline(sketch, "E29", {"points": [v(26.8, 16.2) * mm, v(24.74, 15.53) * mm, v(22.93, 13.83) * mm, v(20.79, 13.5) * mm]});
            skFitSpline(sketch, "E30", {"points": [v(20.79, 13.5) * mm, v(18.03, 12.52) * mm, v(15.02, 12.02) * mm, v(12.3, 13.47) * mm]});
            skFitSpline(sketch, "E31", {"points": [v(12.3, 13.47) * mm, v(12.57, 10.82) * mm, v(12.3, 8.02) * mm, v(11.09, 5.81) * mm]});
            skFitSpline(sketch, "E32", {"points": [v(11.09, 5.81) * mm, v(9.7, 2.96) * mm, v(8.19, 0.05) * mm, v(6.1, -1.95) * mm]});
            skFitSpline(sketch, "E33", {"points": [v(6.1, -1.95) * mm, v(4.6, -1.9) * mm, v(3.84, 0.6) * mm, v(2.86, 1.91) * mm]});
            skFitSpline(sketch, "E34", {"points": [v(2.86, 1.91) * mm, v(3.3, -0.2) * mm, v(2.39, -0.7) * mm, v(0.97, -0.64) * mm]});
            skFitSpline(sketch, "E35", {"points": [v(0.97, -0.64) * mm, v(-0.2, -2.05) * mm, v(-1.11, -1.03) * mm, v(-2.04, 0.22) * mm]});
            skFitSpline(sketch, "E36", {"points": [v(-2.04, 0.22) * mm, v(-2.2, -1.62) * mm, v(-0.48, -5.37) * mm, v(-2.17, -5.84) * mm]});
            skFitSpline(sketch, "E37", {"points": [v(-2.17, -5.84) * mm, v(-4.98, -6.11) * mm, v(-7.8, -5.27) * mm, v(-10.49, -4.2) * mm]});
            skFitSpline(sketch, "E38", {"points": [v(-10.49, -4.2) * mm, v(-12.8, -3.14) * mm, v(-14.9, -1.4) * mm, v(-16.92, 0.38) * mm]});
            skFitSpline(sketch, "E39", {"points": [v(-16.92, 0.38) * mm, v(-18.18, -3.03) * mm, v(-20.68, -5.21) * mm, v(-22.94, -7.31) * mm]});
            skFitSpline(sketch, "E40", {"points": [v(-22.94, -7.31) * mm, v(-24.13, -8.25) * mm, v(-25.34, -9.13) * mm, v(-26.6, -9.89) * mm]});
            skFitSpline(sketch, "E41", {"points": [v(-26.8, -9.93) * mm, v(-24.06, -9.73) * mm, v(-21.14, -9.85) * mm, v(-18.75, -11.83) * mm]});
            skFitSpline(sketch, "E42", {"points": [v(-18.75, -11.83) * mm, v(-17.4, -15.04) * mm, v(-15.28, -11.37) * mm, v(-13.35, -11.4) * mm]});
            skFitSpline(sketch, "E43", {"points": [v(-13.35, -11.4) * mm, v(-10.96, -10.95) * mm, v(-8.47, -11.9) * mm, v(-7.18, -14.84) * mm]});
            skFitSpline(sketch, "E44", {"points": [v(-7.18, -14.84) * mm, v(-6.12, -17.91) * mm, v(-4.18, -13.06) * mm, v(-2.43, -13.3) * mm]});
            skFitSpline(sketch, "E45", {"points": [v(-2.43, -13.3) * mm, v(0.8, -12.14) * mm, v(4.36, -13.5) * mm, v(6.96, -16.2) * mm]});
            skFitSpline(sketch, "E46", {"points": [v(6.96, -16.2) * mm, v(6.88, -12.29) * mm, v(9.56, -9.75) * mm, v(11.76, -7.87) * mm]});
            skFitSpline(sketch, "E47", {"points": [v(11.76, -7.87) * mm, v(12.77, -6.28) * mm, v(15.9, -7.9) * mm, v(14.71, -4.9) * mm]});
            skFitSpline(sketch, "E48", {"points": [v(14.71, -4.9) * mm, v(14.58, -1.9) * mm, v(15.05, 1.67) * mm, v(17.2, 3.27) * mm]});
            skFitSpline(sketch, "E49", {"points": [v(17.2, 3.27) * mm, v(18.64, 5.27) * mm, v(21.62, 3.25) * mm, v(21.51, 6.85) * mm]});
            skFitSpline(sketch, "E50", {"points": [v(21.51, 6.85) * mm, v(22.65, 10.42) * mm, v(24.67, 13.3) * mm, v(26.63, 16.12) * mm]});
            skFitSpline(sketch, "E51", {"points": [v(26.63, 16.12) * mm, v(24.57, 15.45) * mm, v(22.76, 13.76) * mm, v(20.62, 13.43) * mm]});
            skFitSpline(sketch, "E52", {"points": [v(20.62, 13.43) * mm, v(17.86, 12.44) * mm, v(14.84, 11.95) * mm, v(12.12, 13.4) * mm]});
            skFitSpline(sketch, "E53", {"points": [v(12.12, 13.4) * mm, v(12.4, 10.74) * mm, v(12.12, 7.94) * mm, v(10.92, 5.73) * mm]});
            skFitSpline(sketch, "E54", {"points": [v(10.92, 5.73) * mm, v(9.53, 2.88) * mm, v(8.02, -0.03) * mm, v(5.94, -2.03) * mm]});
            skFitSpline(sketch, "E55", {"points": [v(5.94, -2.03) * mm, v(4.43, -1.97) * mm, v(3.67, 0.53) * mm, v(2.69, 1.84) * mm]});
            skFitSpline(sketch, "E56", {"points": [v(2.69, 1.84) * mm, v(3.12, -0.28) * mm, v(2.21, -0.77) * mm, v(0.8, -0.71) * mm]});
            skFitSpline(sketch, "E57", {"points": [v(0.8, -0.71) * mm, v(-0.37, -2.13) * mm, v(-1.28, -1.1) * mm, v(-2.21, 0.14) * mm]});
            skFitSpline(sketch, "E58", {"points": [v(-2.21, 0.14) * mm, v(-2.38, -1.7) * mm, v(-0.65, -5.45) * mm, v(-2.34, -5.91) * mm]});
            skFitSpline(sketch, "E59", {"points": [v(-2.34, -5.91) * mm, v(-5.15, -6.2) * mm, v(-7.98, -5.35) * mm, v(-10.66, -4.28) * mm]});
            skFitSpline(sketch, "E60", {"points": [v(-10.66, -4.28) * mm, v(-12.97, -3.22) * mm, v(-15.07, -1.48) * mm, v(-17.1, 0.3) * mm]});
            skFitSpline(sketch, "E61", {"points": [v(-17.1, 0.3) * mm, v(-18.36, -3.1) * mm, v(-20.85, -5.29) * mm, v(-23.11, -7.4) * mm]});
            skFitSpline(sketch, "E62", {"points": [v(-23.11, -7.4) * mm, v(-24.3, -8.33) * mm, v(-25.52, -9.2) * mm, v(-26.77, -9.96) * mm]});
            skFitSpline(sketch, "E63", {"points": [v(-26.63, -8.82) * mm, v(-23.91, -8.64) * mm, v(-21.02, -8.75) * mm, v(-18.64, -10.6) * mm]});
            skFitSpline(sketch, "E64", {"points": [v(-18.64, -10.6) * mm, v(-17.3, -13.58) * mm, v(-15.2, -10.16) * mm, v(-13.3, -10.2) * mm]});
            skFitSpline(sketch, "E65", {"points": [v(-13.3, -10.2) * mm, v(-10.93, -9.77) * mm, v(-8.45, -10.67) * mm, v(-7.18, -13.4) * mm]});
            skFitSpline(sketch, "E66", {"points": [v(-7.18, -13.4) * mm, v(-6.12, -16.26) * mm, v(-4.2, -11.74) * mm, v(-2.46, -11.97) * mm]});
            skFitSpline(sketch, "E67", {"points": [v(-2.46, -11.97) * mm, v(0.74, -10.88) * mm, v(4.27, -12.15) * mm, v(6.85, -14.66) * mm]});
            skFitSpline(sketch, "E68", {"points": [v(6.85, -14.66) * mm, v(6.76, -11.02) * mm, v(9.42, -8.66) * mm, v(11.6, -6.9) * mm]});
            skFitSpline(sketch, "E69", {"points": [v(11.6, -6.9) * mm, v(12.6, -5.43) * mm, v(15.71, -6.93) * mm, v(14.53, -4.15) * mm]});
            skFitSpline(sketch, "E70", {"points": [v(14.53, -4.15) * mm, v(14.4, -1.35) * mm, v(14.86, 1.98) * mm, v(17, 3.46) * mm]});
            skFitSpline(sketch, "E71", {"points": [v(17, 3.46) * mm, v(18.43, 5.33) * mm, v(21.38, 3.45) * mm, v(21.27, 6.8) * mm]});
            skFitSpline(sketch, "E72", {"points": [v(21.27, 6.8) * mm, v(22.4, 10.12) * mm, v(24.4, 12.81) * mm, v(26.34, 15.43) * mm]});
            skFitSpline(sketch, "E73", {"points": [v(26.34, 15.43) * mm, v(24.3, 14.8) * mm, v(22.5, 13.23) * mm, v(20.38, 12.92) * mm]});
            skFitSpline(sketch, "E74", {"points": [v(20.38, 12.92) * mm, v(17.64, 12) * mm, v(14.66, 11.54) * mm, v(11.96, 12.9) * mm]});
            skFitSpline(sketch, "E75", {"points": [v(11.96, 12.9) * mm, v(12.23, 10.42) * mm, v(11.96, 7.81) * mm, v(10.76, 5.76) * mm]});
            skFitSpline(sketch, "E76", {"points": [v(10.76, 5.76) * mm, v(9.4, 3.1) * mm, v(7.89, 0.4) * mm, v(5.83, -1.47) * mm]});
            skFitSpline(sketch, "E77", {"points": [v(5.83, -1.47) * mm, v(4.33, -1.42) * mm, v(3.58, 0.91) * mm, v(2.6, 2.13) * mm]});
            skFitSpline(sketch, "E78", {"points": [v(2.6, 2.13) * mm, v(3.03, 0.16) * mm, v(2.14, -0.3) * mm, v(0.73, -0.24) * mm]});
            skFitSpline(sketch, "E79", {"points": [v(0.73, -0.24) * mm, v(-0.43, -1.56) * mm, v(-1.33, -0.6) * mm, v(-2.25, 0.55) * mm]});
            skFitSpline(sketch, "E80", {"points": [v(-2.25, 0.55) * mm, v(-2.42, -1.16) * mm, v(-0.7, -4.65) * mm, v(-2.38, -5.09) * mm]});
            skFitSpline(sketch, "E81", {"points": [v(-2.38, -5.09) * mm, v(-5.17, -5.34) * mm, v(-7.97, -4.56) * mm, v(-10.63, -3.56) * mm]});
            skFitSpline(sketch, "E82", {"points": [v(-10.63, -3.56) * mm, v(-12.92, -2.58) * mm, v(-15, -0.96) * mm, v(-17, 0.7) * mm]});
            skFitSpline(sketch, "E83", {"points": [v(-17, 0.7) * mm, v(-18.26, -2.47) * mm, v(-20.73, -4.5) * mm, v(-22.97, -6.46) * mm]});
            skFitSpline(sketch, "E84", {"points": [v(-22.97, -6.46) * mm, v(-24.15, -7.33) * mm, v(-25.35, -8.15) * mm, v(-26.6, -8.85) * mm]});
            skLineSegment(sketch, "E85", {"start": v(2.43, -4.8) * mm, "end": v(3.3, -4.35) * mm});
            skLineSegment(sketch, "E86", {"start": v(3.3, -4.35) * mm, "end": v(4.4, -3.14) * mm});
            skLineSegment(sketch, "E87", {"start": v(4.4, -3.14) * mm, "end": v(3.1, -2.42) * mm});
            skLineSegment(sketch, "E88", {"start": v(3.1, -2.42) * mm, "end": v(2.43, -4.8) * mm});
            skLineSegment(sketch, "E89", {"start": v(1.66, -5.2) * mm, "end": v(1.04, -4.29) * mm});
            skLineSegment(sketch, "E90", {"start": v(1.04, -4.29) * mm, "end": v(-0.21, -3.38) * mm});
            skLineSegment(sketch, "E91", {"start": v(-0.21, -3.38) * mm, "end": v(-0.3, -5.2) * mm});
            skLineSegment(sketch, "E92", {"start": v(-0.3, -5.2) * mm, "end": v(1.66, -5.2) * mm});
            skSolve(sketch);
        }
        {
            var Q0;
            {var subQ21=sQuery(id+"F8.wireOp",EDGE,"E32");Q0=makeQuery(id+"F8.imprint","IMPRINT",FACE,{"disambiguationData":[TD([[makeQuery(id+"F8.imprint","IMPRINT",EDGE,{"derivedFrom":subQ21}),1.0]])]});}
            var Q1;
            {var subQ4=sQuery(id+"F8.wireOp",EDGE,"E21");Q1=makeQuery(id+"F8.imprint","IMPRINT",FACE,{"disambiguationData":[TD([[makeQuery(id+"F8.imprint","IMPRINT",EDGE,{"derivedFrom":subQ4}),1.0]])]});}
            extrude(context, id + "F9", {"entities" : qUnion([Q0, Q1]), "operationType" : NewBodyOperationType.REMOVE, "oppositeDirection" : true, "depth" : 0.6 * mm});
        }
    });
